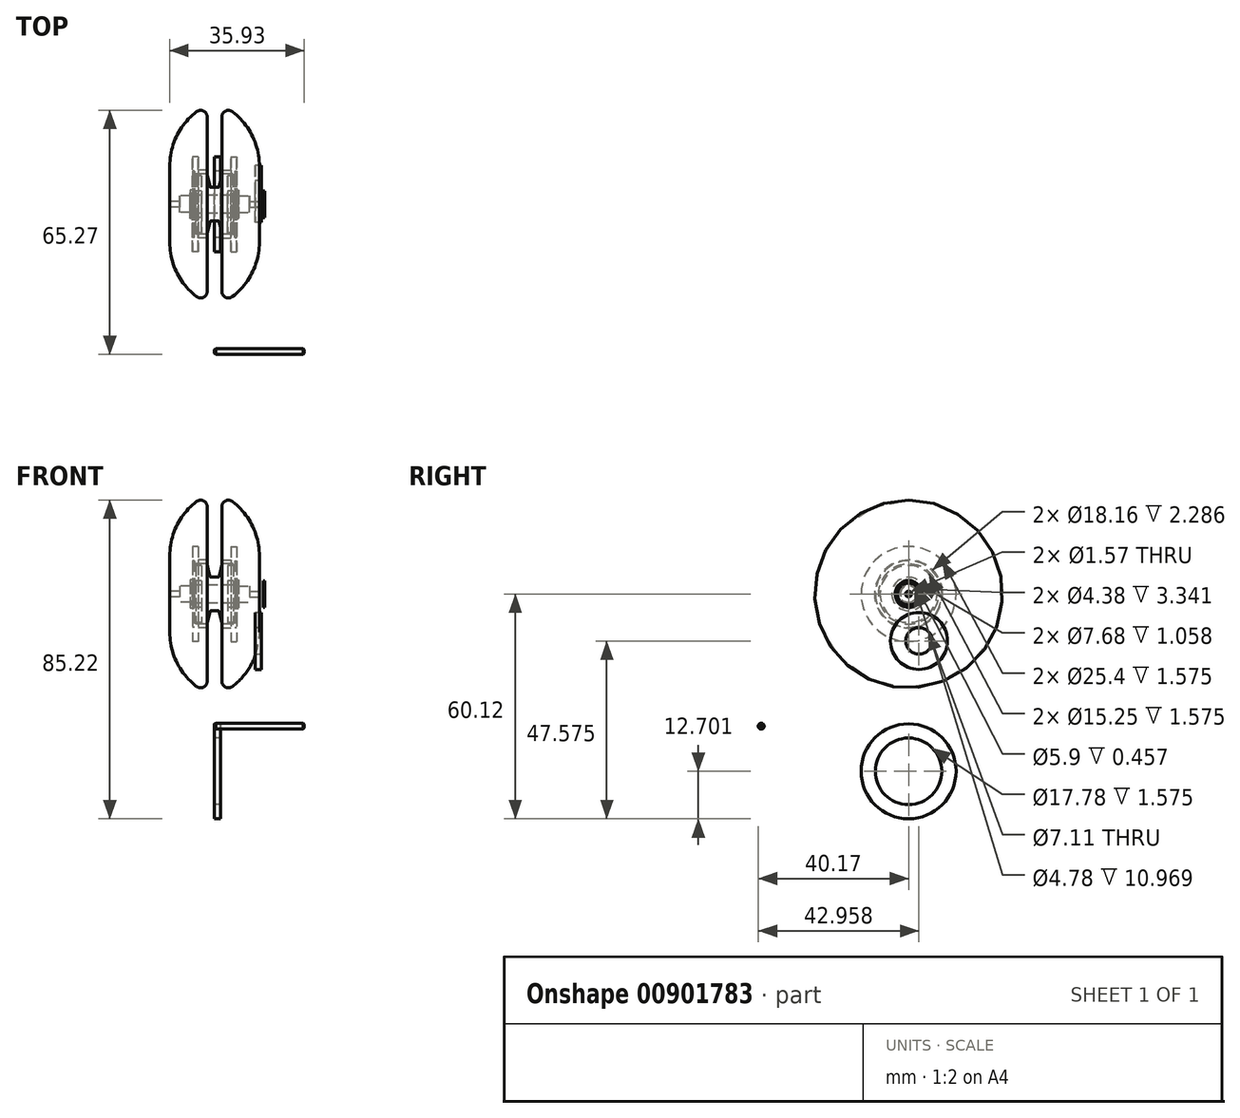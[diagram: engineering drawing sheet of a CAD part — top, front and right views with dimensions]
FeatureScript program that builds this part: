
annotation { "Feature Type Name" : "Feature", "Feature Type Description" : "" }
export const myFeature = defineFeature(function(context is Context, id is Id, definition is map)
    precondition{}
    {
        {
            var Q0;
            Q0=qCreatedBy(makeId("Top.planeOp"),FACE);
            var sketch = newSketch(context, id + "F0", { "sketchPlane" : qUnion([Q0])});
            skLineSegment(sketch, "E0", {"start": v(-43.15, 0) * mm, "end": v(47.7, 0) * mm, "construction": true});
            skLineSegment(sketch, "E1", {"start": v(0, 35.7) * mm, "end": v(0, -27.9) * mm, "construction": true});
            skLineSegment(sketch, "E2", {"start": v(-1.98, 7.95) * mm, "end": v(-1.25, 4.77) * mm});
            skLineSegment(sketch, "E3", {"start": v(-0.9, 4.49) * mm, "end": v(0.9, 4.49) * mm});
            skLineSegment(sketch, "E4", {"start": v(1.25, 4.77) * mm, "end": v(1.98, 7.95) * mm});
            skPoint(sketch, "E5.visualSharp", {"position": v(-1.19, 4.49) * mm});
            skArc(sketch, "E5.filletArc", {"start": v(-1.25, 4.77) * mm, "mid": v(-1.12, 4.57) * mm, "end": v(-0.9, 4.49) * mm});
            skPoint(sketch, "E6.visualSharp", {"position": v(1.19, 4.49) * mm});
            skArc(sketch, "E6.filletArc", {"start": v(0.9, 4.49) * mm, "mid": v(1.12, 4.57) * mm, "end": v(1.25, 4.77) * mm});
            skLineSegment(sketch, "E7", {"start": v(-2.1, 8.05) * mm, "end": v(-4.9, 8.05) * mm});
            skLineSegment(sketch, "E8.MirrorCS", {"start": v(2.1, 8.05) * mm, "end": v(4.9, 8.05) * mm});
            skLineSegment(sketch, "E9.MirrorCS", {"start": v(5.02, 7.92) * mm, "end": v(5.02, 7.62) * mm});
            skPoint(sketch, "E10.visualSharp", {"position": v(-5.02, 8.05) * mm});
            skArc(sketch, "E10.filletArc", {"start": v(-4.9, 8.05) * mm, "mid": v(-4.99, 8.01) * mm, "end": v(-5.02, 7.92) * mm});
            skPoint(sketch, "E11.visualSharp", {"position": v(-2, 8.05) * mm});
            skArc(sketch, "E11.filletArc", {"start": v(-1.98, 7.95) * mm, "mid": v(-2.02, 8.02) * mm, "end": v(-2.1, 8.05) * mm});
            skPoint(sketch, "E12.visualSharp", {"position": v(2, 8.05) * mm});
            skArc(sketch, "E12.filletArc", {"start": v(2.1, 8.05) * mm, "mid": v(2.02, 8.02) * mm, "end": v(1.98, 7.95) * mm});
            skPoint(sketch, "E13.visualSharp", {"position": v(5.02, 8.05) * mm});
            skArc(sketch, "E13.filletArc", {"start": v(5.02, 7.92) * mm, "mid": v(4.99, 8.01) * mm, "end": v(4.9, 8.05) * mm});
            skLineSegment(sketch, "E14", {"start": v(-5.02, 7.92) * mm, "end": v(-5.02, 7.62) * mm});
            skLineSegment(sketch, "E15", {"start": v(-5.02, 7.62) * mm, "end": v(-3.45, 7.62) * mm});
            skLineSegment(sketch, "E16", {"start": v(-3.45, 7.62) * mm, "end": v(-3.45, 3.55) * mm});
            skLineSegment(sketch, "E17", {"start": v(-3.45, 3.55) * mm, "end": v(-5.02, 3.55) * mm});
            skLineSegment(sketch, "E18.MirrorCS", {"start": v(5.02, 7.62) * mm, "end": v(3.45, 7.62) * mm});
            skLineSegment(sketch, "E19.MirrorCS", {"start": v(3.45, 7.62) * mm, "end": v(3.45, 3.55) * mm});
            skLineSegment(sketch, "E20.MirrorCS", {"start": v(3.45, 3.55) * mm, "end": v(5.02, 3.55) * mm});
            skLineSegment(sketch, "E21", {"start": v(-5.48, 2.39) * mm, "end": v(-5.48, 2.95) * mm});
            skLineSegment(sketch, "E22", {"start": v(-5.48, 2.95) * mm, "end": v(-5.02, 2.95) * mm});
            skLineSegment(sketch, "E23", {"start": v(-5.02, 3.55) * mm, "end": v(-5.02, 2.95) * mm});
            skLineSegment(sketch, "E24.MirrorCS", {"start": v(5.02, 3.55) * mm, "end": v(5.02, 2.95) * mm});
            skLineSegment(sketch, "E25.MirrorCS", {"start": v(5.48, 2.95) * mm, "end": v(5.02, 2.95) * mm});
            skLineSegment(sketch, "E26.MirrorCS", {"start": v(5.48, 2.39) * mm, "end": v(5.48, 2.95) * mm});
            skLineSegment(sketch, "E27", {"start": v(-5.48, 2.39) * mm, "end": v(5.48, 2.39) * mm});
            skSolve(sketch);
        }
        {
            var Q0;
            Q0=qCreatedBy(makeId("Right.planeOp"),FACE);
            var sketch = newSketch(context, id + "F1", { "sketchPlane" : qUnion([Q0])});
            skCircle(sketch, "E28", {"center": v(-39.39, -35.37) * mm, "radius": 0.79 * mm});
            skSolve(sketch);
        }
        {
            var Q0;
            Q0 = qSketchRegion(id + "F1", true);
            extrude(context, id + "F2", {"entities" : qUnion([Q0]), "depth" : 33.9 * mm, "offsetDistance" : 25.4 * mm});
        }
        {
            var Q0;
            Q0=makeQuery(id+"F2.opExtrude","CAP_EDGE",EDGE,{"disambiguationData":[OSD([sQuery(id+"F1.wireOp",EDGE,"E28")])],"isStart":false});
            var Q1;
            Q1=makeQuery(id+"F2.opExtrude","CAP_EDGE",EDGE,{"disambiguationData":[OSD([sQuery(id+"F1.wireOp",EDGE,"E28")])],"isStart":true});
            chamfer(context, id + "F3", {"entities" : qUnion([Q0, Q1]), "width" : 0.3 * mm, "tangentPropagation" : true});
        }
        {
            var Q0;
            Q0=qCreatedBy(makeId("Top.planeOp"),FACE);
            var sketch = newSketch(context, id + "F4", { "sketchPlane" : qUnion([Q0])});
            skLineSegment(sketch, "E29", {"start": v(-48.04, 0) * mm, "end": v(12.58, 0) * mm, "construction": true});
            skLineSegment(sketch, "E30", {"start": v(-11.98, 10.2) * mm, "end": v(-11.98, 0.79) * mm});
            skLineSegment(sketch, "E31", {"start": v(-11.98, 0.79) * mm, "end": v(-9.37, 0.79) * mm});
            skLineSegment(sketch, "E32", {"start": v(-9.37, 0.79) * mm, "end": v(-9.37, 2.2) * mm});
            skPoint(sketch, "E33.visualSharp", {"position": v(-1.51, 24.87) * mm});
            skArc(sketch, "E33.filletArc", {"start": v(-1.95, 23.32) * mm, "mid": v(-2.94, 24.91) * mm, "end": v(-4.81, 24.73) * mm});
            skArc(sketch, "E34", {"start": v(-4.81, 24.73) * mm, "mid": v(-10.09, 18.3) * mm, "end": v(-11.98, 10.2) * mm});
            skLineSegment(sketch, "E35", {"start": v(-1.95, 23.32) * mm, "end": v(-1.95, 9.2) * mm});
            skLineSegment(sketch, "E36", {"start": v(-2.08, 9.08) * mm, "end": v(-2.65, 9.08) * mm});
            skLineSegment(sketch, "E37", {"start": v(-6.49, 3.84) * mm, "end": v(-6.49, 2.95) * mm});
            skLineSegment(sketch, "E38", {"start": v(-6.49, 2.95) * mm, "end": v(-6.03, 2.95) * mm});
            skLineSegment(sketch, "E39", {"start": v(-6.03, 2.95) * mm, "end": v(-6.03, 2.2) * mm});
            skLineSegment(sketch, "E40", {"start": v(-5.43, 3.84) * mm, "end": v(-5.43, 8.9) * mm});
            skLineSegment(sketch, "E41", {"start": v(-5.43, 8.9) * mm, "end": v(-5.94, 8.9) * mm});
            skLineSegment(sketch, "E42", {"start": v(-5.94, 8.9) * mm, "end": v(-5.94, 12.7) * mm});
            skLineSegment(sketch, "E43", {"start": v(-5.94, 12.7) * mm, "end": v(-4.36, 12.7) * mm});
            skLineSegment(sketch, "E44", {"start": v(-4.36, 9.2) * mm, "end": v(-4.36, 12.7) * mm});
            skLineSegment(sketch, "E45", {"start": v(-4.26, 9.08) * mm, "end": v(-2.65, 9.08) * mm});
            skPoint(sketch, "E46.visualSharp", {"position": v(-1.95, 9.08) * mm});
            skArc(sketch, "E46.filletArc", {"start": v(-2.08, 9.08) * mm, "mid": v(-1.99, 9.12) * mm, "end": v(-1.95, 9.2) * mm});
            skPoint(sketch, "E47.visualSharp", {"position": v(-4.36, 9.08) * mm});
            skLineSegment(sketch, "E48", {"start": v(-6.49, 3.84) * mm, "end": v(-5.43, 3.84) * mm});
            skLineSegment(sketch, "E49", {"start": v(-4.36, 9.2) * mm, "end": v(-4.36, 9.08) * mm});
            skLineSegment(sketch, "E50", {"start": v(-4.26, 9.08) * mm, "end": v(-4.36, 9.08) * mm});
            skLineSegment(sketch, "E51", {"start": v(-9.37, 2.2) * mm, "end": v(-6.03, 2.2) * mm});
            skSolve(sketch);
        }
        {
            var Q0;
            Q0=makeQuery(id+"F4.imprint","IMPRINT",FACE,{"disambiguationData":[TD([[makeQuery(id+"F4.imprint","IMPRINT",EDGE,{"derivedFrom":sQuery(id+"F4.wireOp",EDGE,"E30")}),1.0]])]});
            var Q1;
            Q1=sQuery(id+"F4.wireOp",EDGE,"E29");
            revolve(context, id + "F5", {"surfaceOperationType" : NewSurfaceOperationType.NEW, "entities" : qUnion([Q0]), "axis" : qUnion([Q1]), "revolveType" : RevolveType.FULL});
        }
        {
            var Q0;
            Q0 = qSketchRegion(id + "F0", true);
            var Q1;
            Q1=sQuery(id+"F0.wireOp",EDGE,"E0");
            revolve(context, id + "F6", {"surfaceOperationType" : NewSurfaceOperationType.NEW, "entities" : qUnion([Q0]), "axis" : qUnion([Q1]), "revolveType" : RevolveType.FULL});
        }
        {
            var Q0;
            Q0=makeQuery(id+"F2.opExtrude","SWEPT_BODY",BODY,{"disambiguationData":[OSD([sQuery(id+"F1.wireOp",EDGE,"E28")])]});
            deleteBodies(context, id + "F7", {"entities" : qUnion([Q0])});
        }
        {
            var Q0;
            Q0=makeQuery(id+"F5.opRevolve","SWEPT_BODY",BODY,{"disambiguationData":[OSD([sQuery(id+"F4.wireOp",EDGE,"E30"),sQuery(id+"F4.wireOp",EDGE,"E31"),sQuery(id+"F4.wireOp",EDGE,"E32"),sQuery(id+"F4.wireOp",EDGE,"E33.filletArc"),sQuery(id+"F4.wireOp",EDGE,"E34"),sQuery(id+"F4.wireOp",EDGE,"E35"),sQuery(id+"F4.wireOp",EDGE,"E36"),sQuery(id+"F4.wireOp",EDGE,"da237736-d7f9-4b6c-b57e-93ea38959bfb"),sQuery(id+"F4.wireOp",EDGE,"E37"),sQuery(id+"F4.wireOp",EDGE,"E38"),sQuery(id+"F4.wireOp",EDGE,"E39"),sQuery(id+"F4.wireOp",EDGE,"KE9W3pVK-VeS7-iO4B-E9TI-OXFRdq51j9FU"),sQuery(id+"F4.wireOp",EDGE,"E40"),sQuery(id+"F4.wireOp",EDGE,"E41"),sQuery(id+"F4.wireOp",EDGE,"E42"),sQuery(id+"F4.wireOp",EDGE,"E43"),sQuery(id+"F4.wireOp",EDGE,"E44"),sQuery(id+"F4.wireOp",EDGE,"E45"),sQuery(id+"F4.wireOp",EDGE,"E46.filletArc"),sQuery(id+"F4.wireOp",EDGE,"E47.filletArc"),sQuery(id+"F4.wireOp",EDGE,"E48")])]});
            var Q1;
            Q1=qCreatedBy(makeId("Right.planeOp"),FACE);
            mirror(context, id + "F8", {"entities" : qUnion([Q0]), "mirrorPlane" : qUnion([Q1])});
        }
        {
            var Q0;
            Q0=makeQuery(id+"F6.opRevolve","SWEPT_FACE",FACE,{"disambiguationData":[OSD([sQuery(id+"F0.wireOp",EDGE,"E19.MirrorCS")])]});
            var sketch = newSketch(context, id + "F9", { "sketchPlane" : qUnion([Q0])});
            skCircle(sketch, "E52.0", {"center": v(2.79, -34.82) * mm, "radius": 7.62 * mm});
            skCircle(sketch, "E53.0", {"center": v(2.79, -34.82) * mm, "radius": 3.55 * mm});
            skSolve(sketch);
        }
        {
            var Q0;
            Q0=makeQuery(id+"F9.imprint","IMPRINT",FACE,{"disambiguationData":[TD([[makeQuery(id+"F9.imprint","IMPRINT",EDGE,{"derivedFrom":sQuery(id+"F9.wireOp",EDGE,"E52.0")}),1.0]])]});
            extrude(context, id + "F10", {"entities" : qUnion([Q0]), "depth" : 1.57 * mm, "offsetDistance" : 25.4 * mm});
        }
        {
            var Q0;
            Q0=makeQuery(id+"F10.opExtrude","SWEPT_BODY",BODY,{"disambiguationData":[OSD([sQuery(id+"F0.wireOp",EDGE,"E18.MirrorCS"),sQuery(id+"F0.wireOp",EDGE,"E19.MirrorCS"),sQuery(id+"F0.wireOp",EDGE,"E20.MirrorCS"),sQuery(id+"F9.wireOp",EDGE,"E52.0")])]});
            var Q1;
            Q1=sQuery(id+"F4.wireOp",EDGE,"E29");
            transform(context, id + "F11", {"entities" : qUnion([Q0]), "transformType" : TransformType.TRANSLATION_3D, "dx" : 7.44 * mm, "dy" : 0 * mm, "dz" : 0 * mm, "makeCopy" : false});
        }
        {
            var Q0;
            Q0=makeQuery(id+"F6.opRevolve","SWEPT_FACE",FACE,{"disambiguationData":[OSD([sQuery(id+"F0.wireOp",EDGE,"E24.MirrorCS")])]});
            var sketch = newSketch(context, id + "F12", { "sketchPlane" : qUnion([Q0])});
            skCircle(sketch, "E54.0", {"center": v(0, 0) * mm, "radius": 2.95 * mm});
            skCircle(sketch, "E55.0", {"center": v(0, 0) * mm, "radius": 3.55 * mm});
            skSolve(sketch);
        }
        {
            var Q0;
            Q0=makeQuery(id+"F12.imprint","IMPRINT",FACE,{"disambiguationData":[TD([[makeQuery(id+"F12.imprint","IMPRINT",EDGE,{"derivedFrom":sQuery(id+"F12.wireOp",EDGE,"E54.0")}),1.0]])]});
            extrude(context, id + "F13", {"entities" : qUnion([Q0]), "depth" : 0.46 * mm, "offsetDistance" : 25.4 * mm});
        }
        {
            var Q0;
            Q0=makeQuery(id+"F13.opExtrude","SWEPT_BODY",BODY,{"disambiguationData":[OSD([sQuery(id+"F12.wireOp",EDGE,"E54.0"),sQuery(id+"F12.wireOp",EDGE,"E55.0")])]});
            transform(context, id + "F14", {"entities" : qUnion([Q0]), "transformType" : TransformType.TRANSLATION_3D, "dx" : 7.95 * mm, "dy" : 0 * mm, "dz" : 0 * mm, "makeCopy" : false});
        }
        {
            var Q0;
            Q0=makeQuery(id+"F10.opExtrude","SWEPT_BODY",BODY,{"disambiguationData":[OSD([sQuery(id+"F9.wireOp",EDGE,"E52.0"),sQuery(id+"F9.wireOp",EDGE,"E53.0")])]});
            transform(context, id + "F15", {"entities" : qUnion([Q0]), "transformType" : TransformType.TRANSLATION_3D, "dx" : 0 * mm, "dy" : 0 * mm, "dz" : 22.28 * mm, "makeCopy" : false});
        }
        {
            var Q0;
            Q0=qCreatedBy(makeId("Right.planeOp"),FACE);
            var sketch = newSketch(context, id + "F16", { "sketchPlane" : qUnion([Q0])});
            skCircle(sketch, "E56", {"center": v(0, -47.42) * mm, "radius": 8.9 * mm});
            skCircle(sketch, "E57", {"center": v(0, -47.42) * mm, "radius": 12.7 * mm});
            skSolve(sketch);
        }
        {
            var Q0;
            Q0=makeQuery(id+"F16.imprint","IMPRINT",FACE,{"disambiguationData":[TD([[makeQuery(id+"F16.imprint","IMPRINT",EDGE,{"derivedFrom":sQuery(id+"F16.wireOp",EDGE,"E56")}),-1.0]])]});
            extrude(context, id + "F17", {"entities" : qUnion([Q0]), "depth" : 1.57 * mm, "offsetDistance" : 25.4 * mm});
        }
        {
            var Q0;
            Q0 = qSketchRegion(id + "F1", true);
            extrude(context, id + "F18", {"entities" : qUnion([Q0]), "depth" : 23.95 * mm, "offsetDistance" : 25.4 * mm});
        }
        {
            var Q0;
            Q0=makeQuery(id+"F18.opExtrude","CAP_EDGE",EDGE,{"disambiguationData":[OSD([sQuery(id+"F1.wireOp",EDGE,"E28")])],"isStart":false});
            var Q1;
            Q1=makeQuery(id+"F18.opExtrude","CAP_EDGE",EDGE,{"disambiguationData":[OSD([sQuery(id+"F1.wireOp",EDGE,"E28")])],"isStart":true});
            chamfer(context, id + "F19", {"entities" : qUnion([Q0, Q1]), "width" : 0.3 * mm, "tangentPropagation" : true});
        }
    });
